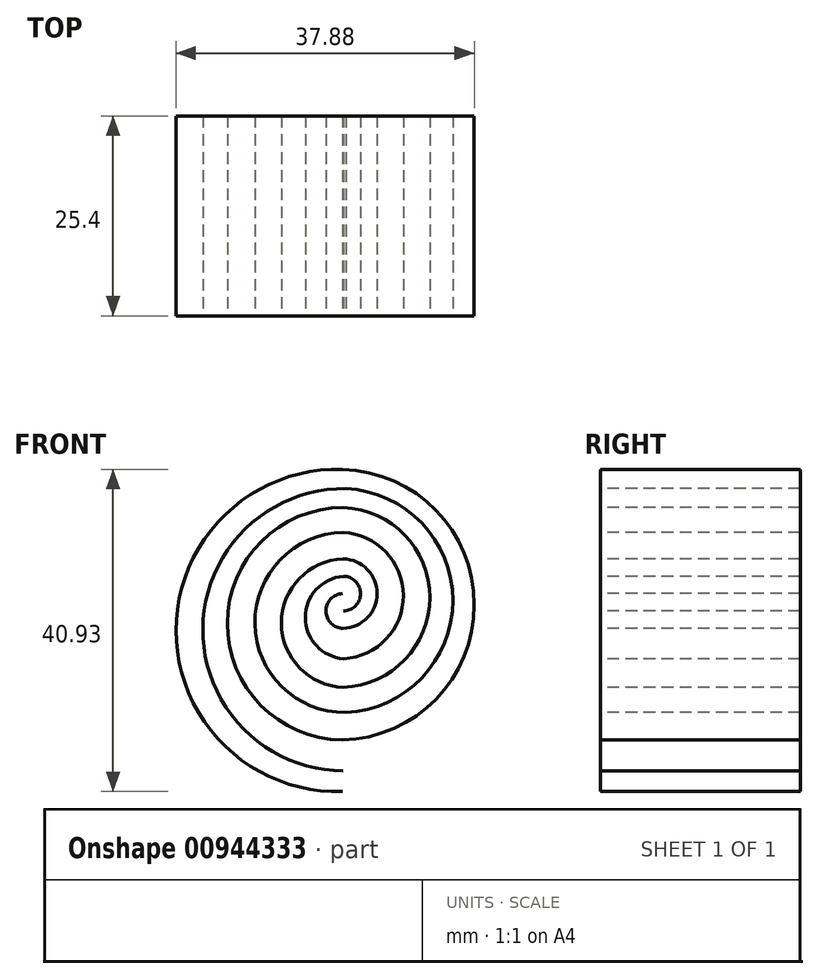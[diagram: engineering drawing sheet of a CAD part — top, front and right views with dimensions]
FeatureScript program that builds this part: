
annotation { "Feature Type Name" : "Feature", "Feature Type Description" : "" }
export const myFeature = defineFeature(function(context is Context, id is Id, definition is map)
    precondition{}
    {
        {
            var Q0;
            Q0=qCreatedBy(makeId("Front.planeOp"),FACE);
            var sketch = newSketch(context, id + "F0", { "sketchPlane" : qUnion([Q0])});
            skArc(sketch, "E0", {"start": v(0, 0) * mm, "mid": v(4.3, 4.41) * mm, "end": v(0, 8.82) * mm});
            skArc(sketch, "E1", {"start": v(0, 8.82) * mm, "mid": v(-7.85, 0.66) * mm, "end": v(0, -7.5) * mm});
            skArc(sketch, "E2", {"start": v(0, -7.5) * mm, "mid": v(11, 3.92) * mm, "end": v(0, 15.35) * mm});
            skArc(sketch, "E3", {"start": v(0, 15.35) * mm, "mid": v(-14.73, 0.64) * mm, "end": v(-0.12, -14.2) * mm});
            skArc(sketch, "E4", {"start": v(-0.12, -14.2) * mm, "mid": v(16.64, 3) * mm, "end": v(-0.12, 20.18) * mm});
            skArc(sketch, "E5", {"start": v(-0.12, 20.18) * mm, "mid": v(-21.24, -0.27) * mm, "end": v(-0.12, -20.72) * mm});
            skArc(sketch, "E6", {"start": v(-0.12, 4.41) * mm, "mid": v(-2.2, 2.15) * mm, "end": v(0, 0) * mm});
            skArc(sketch, "E7", {"start": v(0.01, 2.2) * mm, "mid": v(2.2, 4.41) * mm, "end": v(0.01, 6.62) * mm});
            skArc(sketch, "E8", {"start": v(0.01, 6.62) * mm, "mid": v(-4.82, 1.36) * mm, "end": v(0.04, -3.86) * mm});
            skArc(sketch, "E9", {"start": v(0.04, -3.86) * mm, "mid": v(7.64, 4.17) * mm, "end": v(0, 12.17) * mm});
            skArc(sketch, "E10", {"start": v(0, 12.17) * mm, "mid": v(-11.23, 0.58) * mm, "end": v(0.32, -10.69) * mm});
            skArc(sketch, "E11", {"start": v(0.32, -10.69) * mm, "mid": v(13.92, 3.53) * mm, "end": v(0.32, 17.74) * mm});
            skArc(sketch, "E12", {"start": v(0.32, 17.74) * mm, "mid": v(-17.83, -0.03) * mm, "end": v(0, -18.12) * mm});
            skSolve(sketch);
        }
        {
            var Q0;
            Q0=sQuery(id+"F0.wireOp",EDGE,"E5");
            var Q1;
            Q1=sQuery(id+"F0.wireOp",EDGE,"E12");
            var Q2;
            Q2=sQuery(id+"F0.wireOp",EDGE,"E3");
            var Q3;
            Q3=sQuery(id+"F0.wireOp",EDGE,"E10");
            var Q4;
            Q4=sQuery(id+"F0.wireOp",EDGE,"E1");
            var Q5;
            Q5=sQuery(id+"F0.wireOp",EDGE,"E8");
            var Q6;
            Q6=sQuery(id+"F0.wireOp",EDGE,"E6");
            var Q7;
            Q7=sQuery(id+"F0.wireOp",EDGE,"E7");
            var Q8;
            Q8=sQuery(id+"F0.wireOp",EDGE,"E0");
            var Q9;
            Q9=sQuery(id+"F0.wireOp",EDGE,"E9");
            var Q10;
            Q10=sQuery(id+"F0.wireOp",EDGE,"E2");
            var Q11;
            Q11=sQuery(id+"F0.wireOp",EDGE,"E11");
            var Q12;
            Q12=sQuery(id+"F0.wireOp",EDGE,"E4");
            extrude(context, id + "F1", {"bodyType" : ToolBodyType.SURFACE, "surfaceEntities" : qUnion([Q0, Q1, Q2, Q3, Q4, Q5, Q6, Q7, Q8, Q9, Q10, Q11, Q12]), "depth" : 25.4 * mm, "offsetDistance" : 25.4 * mm});
        }
    });
